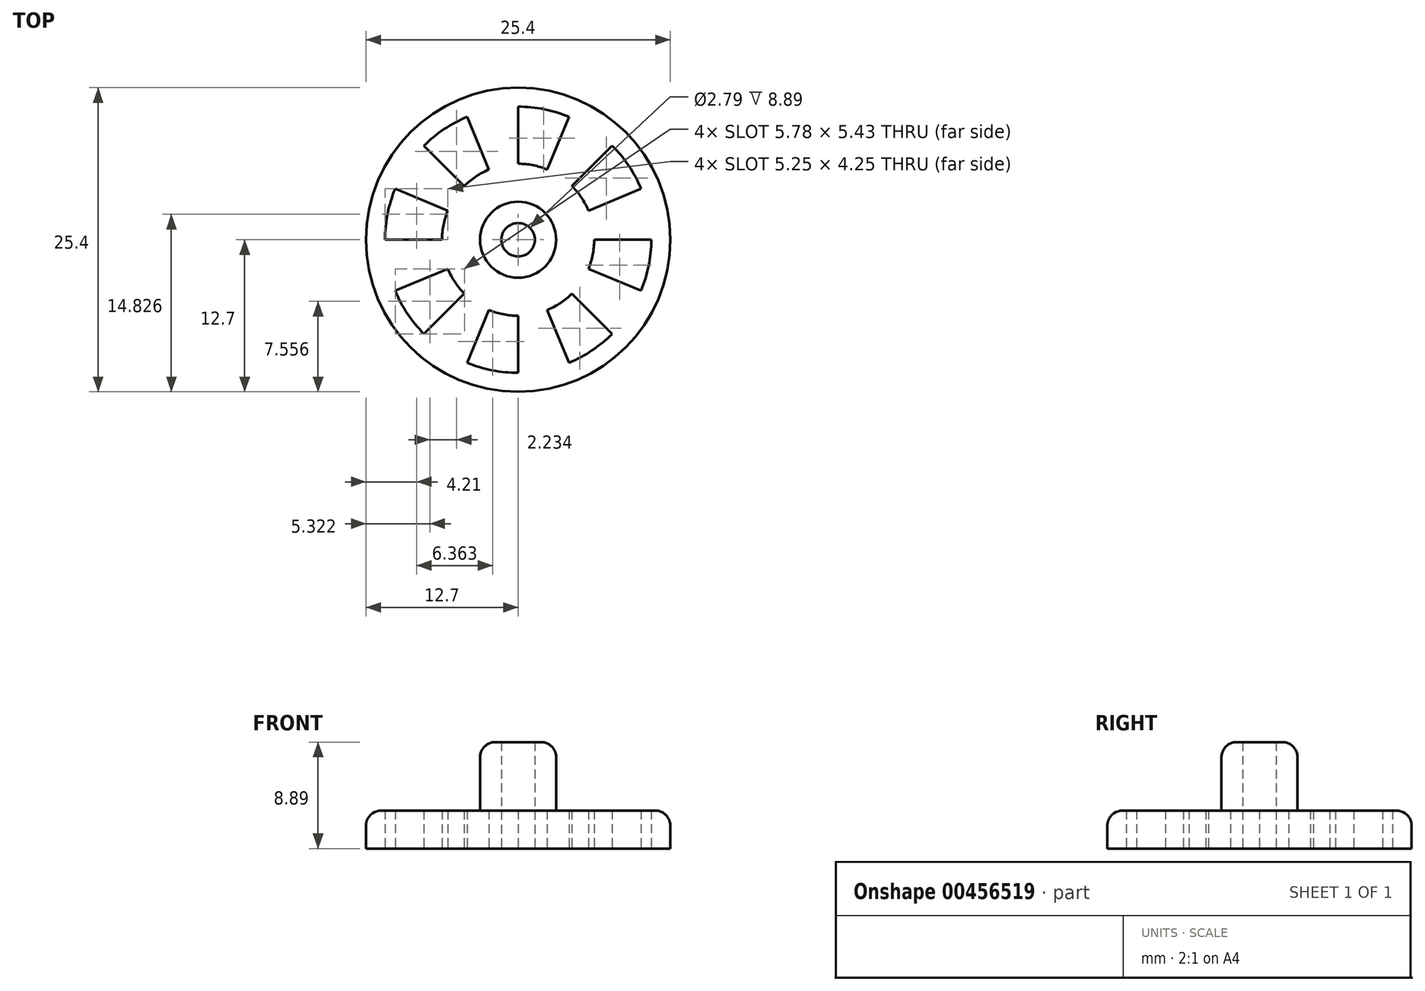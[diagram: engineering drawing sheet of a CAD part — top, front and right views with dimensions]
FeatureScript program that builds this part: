
annotation { "Feature Type Name" : "Feature", "Feature Type Description" : "" }
export const myFeature = defineFeature(function(context is Context, id is Id, definition is map)
    precondition{}
    {
        {
            var Q0;
            Q0=qCreatedBy(makeId("Top.planeOp"),FACE);
            var sketch = newSketch(context, id + "F0", { "sketchPlane" : qUnion([Q0])});
            skCircle(sketch, "E0", {"center": v(0, 0) * mm, "radius": 12.7 * mm});
            skSolve(sketch);
        }
        {
            var Q0;
            Q0=qSketchRegion(id+"F0",true);
            extrude(context, id + "F1", {"entities" : qUnion([Q0]), "depth" : 3.17 * mm});
        }
        {
            var Q0;
            Q0=makeQuery(id+"F1.opExtrude","CAP_FACE",FACE,{"disambiguationData":[OSD([sQuery(id+"F0.wireOp",EDGE,"E0")])],"isStart":false});
            var sketch = newSketch(context, id + "F2", { "sketchPlane" : qUnion([Q0])});
            skCircle(sketch, "E1", {"center": v(0, 0) * mm, "radius": 3.18 * mm});
            skSolve(sketch);
        }
        {
            var Q0;
            Q0=qSketchRegion(id+"F2",true);
            extrude(context, id + "F3", {"entities" : qUnion([Q0]), "operationType" : NewBodyOperationType.ADD, "depth" : 5.7 * mm});
        }
        {
            var Q0;
            Q0=makeQuery(id+"F1.opExtrude","CAP_FACE",FACE,{"disambiguationData":[OSD([sQuery(id+"F0.wireOp",EDGE,"E0")])],"isStart":true});
            var sketch = newSketch(context, id + "F4", { "sketchPlane" : qUnion([Q0])});
            skCircle(sketch, "E2", {"center": v(0, 0) * mm, "radius": 0.95 * mm});
            skSolve(sketch);
        }
        {
            var Q0;
            Q0=qSketchRegion(id+"F4",true);
            extrude(context, id + "F5", {"entities" : qUnion([Q0]), "operationType" : NewBodyOperationType.REMOVE, "oppositeDirection" : true, "depth" : 25.4 * mm});
        }
        {
            var Q0;
            Q0=makeQuery(id+"F1.opExtrude","CAP_FACE",FACE,{"disambiguationData":[OSD([sQuery(id+"F0.wireOp",EDGE,"E0")])],"isStart":true});
            var sketch = newSketch(context, id + "F6", { "sketchPlane" : qUnion([Q0])});
            skCircle(sketch, "E3.0", {"center": v(0, 0) * mm, "radius": 12.7 * mm, "construction": true});
            skCircle(sketch, "E4.0", {"center": v(0, 0) * mm, "radius": 3.18 * mm, "construction": true});
            skCircle(sketch, "E5", {"center": v(0, 0) * mm, "radius": 11.11 * mm});
            skCircle(sketch, "E6", {"center": v(0, 0) * mm, "radius": 6.35 * mm});
            skSolve(sketch);
        }
        {
            var Q0;
            Q0=makeQuery(id+"F6.imprint","IMPRINT",FACE,{"disambiguationData":[TD([[makeQuery(id+"F6.imprint","IMPRINT",EDGE,{"derivedFrom":sQuery(id+"F6.wireOp",EDGE,"E5")}),1.0]])]});
            extrude(context, id + "F7", {"entities" : qUnion([Q0]), "operationType" : NewBodyOperationType.REMOVE, "oppositeDirection" : true, "depth" : 25.4 * mm});
        }
        {
            var Q0;
            Q0=makeQuery(id+"F7.boolean.opBoolean","SPLIT",FACE,{"disambiguationData":[TD([makeQuery(id+"F5.boolean.opBoolean","COPY",FACE,{"derivedFrom":makeQuery(id+"F5.opExtrude","SWEPT_FACE",FACE,{"disambiguationData":[OSD([sQuery(id+"F4.wireOp",EDGE,"E2")])]})})])],"derivedFrom":makeQuery(id+"F1.opExtrude","CAP_FACE",FACE,{"disambiguationData":[OSD([sQuery(id+"F0.wireOp",EDGE,"E0")])],"isStart":true})});
            var sketch = newSketch(context, id + "F8", { "sketchPlane" : qUnion([Q0])});
            skCircle(sketch, "E7.0.0", {"center": v(0, 0) * mm, "radius": 6.35 * mm, "construction": true});
            skCircle(sketch, "E8.0.0", {"center": v(0, 0) * mm, "radius": 12.7 * mm, "construction": true});
            skLineSegment(sketch, "E9", {"start": v(0, 0) * mm, "end": v(0, 12.7) * mm, "construction": true});
            skLineSegment(sketch, "E10", {"start": v(0, 12.7) * mm, "end": v(-12.7, 0) * mm, "construction": true});
            skLineSegment(sketch, "E11", {"start": v(-12.7, 0) * mm, "end": v(0, 0) * mm});
            skLineSegment(sketch, "E12", {"start": v(0, 0) * mm, "end": v(-6.35, 6.35) * mm, "construction": true});
            skLineSegment(sketch, "E13", {"start": v(-6.35, 6.35) * mm, "end": v(-8.98, 8.98) * mm, "construction": true});
            skLineSegment(sketch, "E14", {"start": v(-8.98, 8.98) * mm, "end": v(-12.7, 0) * mm, "construction": true});
            skLineSegment(sketch, "E15", {"start": v(0, 0) * mm, "end": v(-10.84, 4.5) * mm});
            skLineSegment(sketch, "E16", {"start": v(-10.84, 4.5) * mm, "end": v(-11.73, 4.86) * mm});
            skLineSegment(sketch, "E17", {"start": v(-11.73, 4.86) * mm, "end": v(-12.7, 0) * mm});
            skLineSegment(sketch, "E18.1.0", {"start": v(0, 0) * mm, "end": v(-10.84, -4.5) * mm});
            skLineSegment(sketch, "E18.1.1", {"start": v(-10.84, -4.5) * mm, "end": v(-11.73, -4.86) * mm});
            skLineSegment(sketch, "E18.1.2", {"start": v(-11.73, -4.86) * mm, "end": v(-8.98, -8.98) * mm});
            skLineSegment(sketch, "E18.1.3", {"start": v(-8.98, -8.98) * mm, "end": v(0, 0) * mm});
            skLineSegment(sketch, "E18.2.0", {"start": v(0, 0) * mm, "end": v(-4.5, -10.84) * mm});
            skLineSegment(sketch, "E18.2.1", {"start": v(-4.5, -10.84) * mm, "end": v(-4.86, -11.73) * mm});
            skLineSegment(sketch, "E18.2.2", {"start": v(-4.86, -11.73) * mm, "end": v(0, -12.7) * mm});
            skLineSegment(sketch, "E18.2.3", {"start": v(0, -12.7) * mm, "end": v(0, 0) * mm});
            skLineSegment(sketch, "E18.3.0", {"start": v(0, 0) * mm, "end": v(4.5, -10.84) * mm});
            skLineSegment(sketch, "E18.3.1", {"start": v(4.5, -10.84) * mm, "end": v(4.86, -11.73) * mm});
            skLineSegment(sketch, "E18.3.2", {"start": v(4.86, -11.73) * mm, "end": v(8.98, -8.98) * mm});
            skLineSegment(sketch, "E18.3.3", {"start": v(8.98, -8.98) * mm, "end": v(0, 0) * mm});
            skLineSegment(sketch, "E18.4.0", {"start": v(0, 0) * mm, "end": v(10.84, -4.5) * mm});
            skLineSegment(sketch, "E18.4.1", {"start": v(10.84, -4.5) * mm, "end": v(11.73, -4.86) * mm});
            skLineSegment(sketch, "E18.4.2", {"start": v(11.73, -4.86) * mm, "end": v(12.7, 0) * mm});
            skLineSegment(sketch, "E18.4.3", {"start": v(12.7, 0) * mm, "end": v(0, 0) * mm});
            skLineSegment(sketch, "E18.5.0", {"start": v(0, 0) * mm, "end": v(10.84, 4.5) * mm});
            skLineSegment(sketch, "E18.5.1", {"start": v(10.84, 4.5) * mm, "end": v(11.73, 4.86) * mm});
            skLineSegment(sketch, "E18.5.2", {"start": v(11.73, 4.86) * mm, "end": v(8.98, 8.98) * mm});
            skLineSegment(sketch, "E18.5.3", {"start": v(8.98, 8.98) * mm, "end": v(0, 0) * mm});
            skLineSegment(sketch, "E18.6.0", {"start": v(0, 0) * mm, "end": v(4.5, 10.84) * mm});
            skLineSegment(sketch, "E18.6.1", {"start": v(4.5, 10.84) * mm, "end": v(4.86, 11.73) * mm});
            skLineSegment(sketch, "E18.6.2", {"start": v(4.86, 11.73) * mm, "end": v(0, 12.7) * mm});
            skLineSegment(sketch, "E18.6.3", {"start": v(0, 12.7) * mm, "end": v(0, 0) * mm});
            skLineSegment(sketch, "E18.7.0", {"start": v(0, 0) * mm, "end": v(-4.5, 10.84) * mm});
            skLineSegment(sketch, "E18.7.1", {"start": v(-4.5, 10.84) * mm, "end": v(-4.86, 11.73) * mm});
            skLineSegment(sketch, "E18.7.2", {"start": v(-4.86, 11.73) * mm, "end": v(-8.98, 8.98) * mm});
            skLineSegment(sketch, "E18.7.3", {"start": v(-8.98, 8.98) * mm, "end": v(0, 0) * mm});
            skSolve(sketch);
        }
        {
            var Q0;
            {var subQ4=sQuery(id+"F8.wireOp",EDGE,"E18.7.1");Q0=makeQuery(id+"F8.imprint","IMPRINT",FACE,{"disambiguationData":[TD([[makeQuery(id+"F8.imprint","IMPRINT",EDGE,{"derivedFrom":subQ4}),1.0]])]});}
            var Q1;
            {var subQ1=sQuery(id+"F8.wireOp",EDGE,"E16");Q1=makeQuery(id+"F8.imprint","IMPRINT",FACE,{"disambiguationData":[TD([[makeQuery(id+"F8.imprint","IMPRINT",EDGE,{"derivedFrom":subQ1}),1.0]])]});}
            var Q2;
            {var subQ4=sQuery(id+"F8.wireOp",EDGE,"E18.1.1");Q2=makeQuery(id+"F8.imprint","IMPRINT",FACE,{"disambiguationData":[TD([[makeQuery(id+"F8.imprint","IMPRINT",EDGE,{"derivedFrom":subQ4}),1.0]])]});}
            var Q3;
            {var subQ4=sQuery(id+"F8.wireOp",EDGE,"E18.2.1");Q3=makeQuery(id+"F8.imprint","IMPRINT",FACE,{"disambiguationData":[TD([[makeQuery(id+"F8.imprint","IMPRINT",EDGE,{"derivedFrom":subQ4}),1.0]])]});}
            var Q4;
            {var subQ4=sQuery(id+"F8.wireOp",EDGE,"E18.3.1");Q4=makeQuery(id+"F8.imprint","IMPRINT",FACE,{"disambiguationData":[TD([[makeQuery(id+"F8.imprint","IMPRINT",EDGE,{"derivedFrom":subQ4}),1.0]])]});}
            var Q5;
            {var subQ4=sQuery(id+"F8.wireOp",EDGE,"E18.5.1");Q5=makeQuery(id+"F8.imprint","IMPRINT",FACE,{"disambiguationData":[TD([[makeQuery(id+"F8.imprint","IMPRINT",EDGE,{"derivedFrom":subQ4}),1.0]])]});}
            var Q6;
            {var subQ6=sQuery(id+"F8.wireOp",EDGE,"E18.6.1");Q6=makeQuery(id+"F8.imprint","IMPRINT",FACE,{"disambiguationData":[TD([[makeQuery(id+"F8.imprint","IMPRINT",EDGE,{"derivedFrom":subQ6}),1.0]])]});}
            var Q7;
            {var subQ6=sQuery(id+"F8.wireOp",EDGE,"E18.4.1");Q7=makeQuery(id+"F8.imprint","IMPRINT",FACE,{"disambiguationData":[TD([[makeQuery(id+"F8.imprint","IMPRINT",EDGE,{"derivedFrom":subQ6}),1.0]])]});}
            var Q8;
            Q8=makeQuery(id+"F7.boolean.opBoolean","SPLIT",FACE,{"disambiguationData":[TD([makeQuery(id+"F3.opExtrude","SWEPT_FACE",FACE,{"disambiguationData":[OSD([sQuery(id+"F2.wireOp",EDGE,"E1")])]})])],"derivedFrom":makeQuery(id+"F1.opExtrude","CAP_FACE",FACE,{"disambiguationData":[OSD([sQuery(id+"F0.wireOp",EDGE,"E0")])],"isStart":false})});
            extrude(context, id + "F9", {"entities" : qUnion([Q0, Q1, Q2, Q3, Q4, Q5, Q6, Q7]), "operationType" : NewBodyOperationType.ADD, "endBound" : BoundingType.UP_TO_SURFACE, "oppositeDirection" : true, "endBoundEntityFace" : qUnion([Q8]), "depth" : 25.4 * mm});
        }
        {
            var Q0;
            Q0=makeQuery(id+"F3.opExtrude","CAP_EDGE",EDGE,{"disambiguationData":[OSD([sQuery(id+"F2.wireOp",EDGE,"E1")])],"isStart":false});
            var Q1;
            Q1=makeQuery(id+"F3.opExtrude","CAP_EDGE",EDGE,{"disambiguationData":[OSD([sQuery(id+"F2.wireOp",EDGE,"E1")])],"isStart":true});
            var Q2;
            Q2=makeQuery(id+"F1.opExtrude","CAP_EDGE",EDGE,{"disambiguationData":[OSD([sQuery(id+"F0.wireOp",EDGE,"E0")])],"isStart":false});
            fillet(context, id + "F10", {"entities" : qUnion([Q0, Q1, Q2]), "radius" : 1.27 * mm, "tangentPropagation" : true, "allowEdgeOverflow" : false});
        }
        {
            var Q0;
            {var subQ0=sQuery(id+"F6.wireOp",EDGE,"E6");var subQ1=sQuery(id+"F0.wireOp",EDGE,"E0");var subQ2=makeQuery(id+"F1.opExtrude","CAP_FACE",FACE,{"disambiguationData":[OSD([subQ1])],"isStart":true});Q0=makeQuery(id+"F9.boolean.opBoolean","MERGE",FACE,{"derivedFrom":[makeQuery(id+"F7.boolean.opBoolean","SPLIT",FACE,{"disambiguationData":[TD([makeQuery(id+"F1.opExtrude","SWEPT_FACE",FACE,{"disambiguationData":[OSD([subQ1])]})])],"derivedFrom":subQ2}),makeQuery(id+"F7.boolean.opBoolean","SPLIT",FACE,{"disambiguationData":[TD([makeQuery(id+"F5.boolean.opBoolean","COPY",FACE,{"derivedFrom":makeQuery(id+"F5.opExtrude","SWEPT_FACE",FACE,{"disambiguationData":[OSD([sQuery(id+"F4.wireOp",EDGE,"E2")])]})})])],"derivedFrom":subQ2}),makeQuery(id+"F9.opExtrude","CAP_FACE",FACE,{"disambiguationData":[OSD([subQ0,sQuery(id+"F8.wireOp",EDGE,"E11"),sQuery(id+"F8.wireOp",EDGE,"E15"),sQuery(id+"F8.wireOp",EDGE,"E16"),sQuery(id+"F8.wireOp",EDGE,"E17")])],"isStart":true}),makeQuery(id+"F9.opExtrude","CAP_FACE",FACE,{"disambiguationData":[OSD([subQ0,sQuery(id+"F8.wireOp",EDGE,"E18.1.0"),sQuery(id+"F8.wireOp",EDGE,"E18.1.1"),sQuery(id+"F8.wireOp",EDGE,"E18.1.2"),sQuery(id+"F8.wireOp",EDGE,"E18.1.3")])],"isStart":true}),makeQuery(id+"F9.opExtrude","CAP_FACE",FACE,{"disambiguationData":[OSD([subQ0,sQuery(id+"F8.wireOp",EDGE,"E18.2.0"),sQuery(id+"F8.wireOp",EDGE,"E18.2.1"),sQuery(id+"F8.wireOp",EDGE,"E18.2.2"),sQuery(id+"F8.wireOp",EDGE,"E18.2.3")])],"isStart":true}),makeQuery(id+"F9.opExtrude","CAP_FACE",FACE,{"disambiguationData":[OSD([subQ0,sQuery(id+"F8.wireOp",EDGE,"E18.3.0"),sQuery(id+"F8.wireOp",EDGE,"E18.3.1"),sQuery(id+"F8.wireOp",EDGE,"E18.3.2"),sQuery(id+"F8.wireOp",EDGE,"E18.3.3")])],"isStart":true}),makeQuery(id+"F9.opExtrude","CAP_FACE",FACE,{"disambiguationData":[OSD([subQ0,sQuery(id+"F8.wireOp",EDGE,"E18.4.0"),sQuery(id+"F8.wireOp",EDGE,"E18.4.1"),sQuery(id+"F8.wireOp",EDGE,"E18.4.2"),sQuery(id+"F8.wireOp",EDGE,"E18.4.3")])],"isStart":true}),makeQuery(id+"F9.opExtrude","CAP_FACE",FACE,{"disambiguationData":[OSD([subQ0,sQuery(id+"F8.wireOp",EDGE,"E18.5.0"),sQuery(id+"F8.wireOp",EDGE,"E18.5.1"),sQuery(id+"F8.wireOp",EDGE,"E18.5.2"),sQuery(id+"F8.wireOp",EDGE,"E18.5.3")])],"isStart":true}),makeQuery(id+"F9.opExtrude","CAP_FACE",FACE,{"disambiguationData":[OSD([subQ0,sQuery(id+"F8.wireOp",EDGE,"E18.6.0"),sQuery(id+"F8.wireOp",EDGE,"E18.6.1"),sQuery(id+"F8.wireOp",EDGE,"E18.6.2"),sQuery(id+"F8.wireOp",EDGE,"E18.6.3")])],"isStart":true}),makeQuery(id+"F9.opExtrude","CAP_FACE",FACE,{"disambiguationData":[OSD([subQ0,sQuery(id+"F8.wireOp",EDGE,"E18.7.0"),sQuery(id+"F8.wireOp",EDGE,"E18.7.1"),sQuery(id+"F8.wireOp",EDGE,"E18.7.2"),sQuery(id+"F8.wireOp",EDGE,"E18.7.3")])],"isStart":true})]});}
            var sketch = newSketch(context, id + "F11", { "sketchPlane" : qUnion([Q0])});
            skCircle(sketch, "E19", {"center": v(0, 0) * mm, "radius": 1.4 * mm});
            skSolve(sketch);
        }
        {
            var Q0;
            Q0=qSketchRegion(id+"F11",true);
            extrude(context, id + "F12", {"entities" : qUnion([Q0]), "operationType" : NewBodyOperationType.REMOVE, "oppositeDirection" : true, "depth" : 25.4 * mm});
        }
    });
